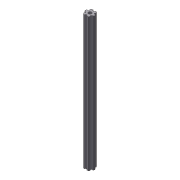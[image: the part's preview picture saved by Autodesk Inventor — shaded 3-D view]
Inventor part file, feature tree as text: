
AUTODESK INVENTOR PART (.ipt)
format: ipt  version: 2012 (Build 160160000, 160)  size: 92,672 bytes
history: native  units: in
note: dims shown in document units (in); Inventor stores cm internally (conversion verified against a paired STEP export)
features: extrude x2, sketch x2, pattern_circular x1
ambient origin geometry x8: Origin, YZ Plane, XZ Plane, XY Plane, X Axis, Y Axis, Z Axis, Center Point
bodies: Solid1 (feature_tree)
feature tree (5):
  extrude  "Extrusion1"  Depth=0.2in
  extrude  "Extrusion2"  Depth=0.0625in
  pattern_circular  "Circular Pattern1"  [2 undecoded]
  sketch  "Sketch1"  dims[d0=0.5in d1=0.2in]
  sketch  "Sketch2"  dims[d2=8.0in d3=0.0in d4=0.0625in d5=3.0in d6=0.0in d7=2.3622in d8=360.0deg]
note: 2 required parameter values undecoded (feature->parameter linkage not recoverable at this tier; creation-order binding heuristic only, values carry confidence <= 0.55)
